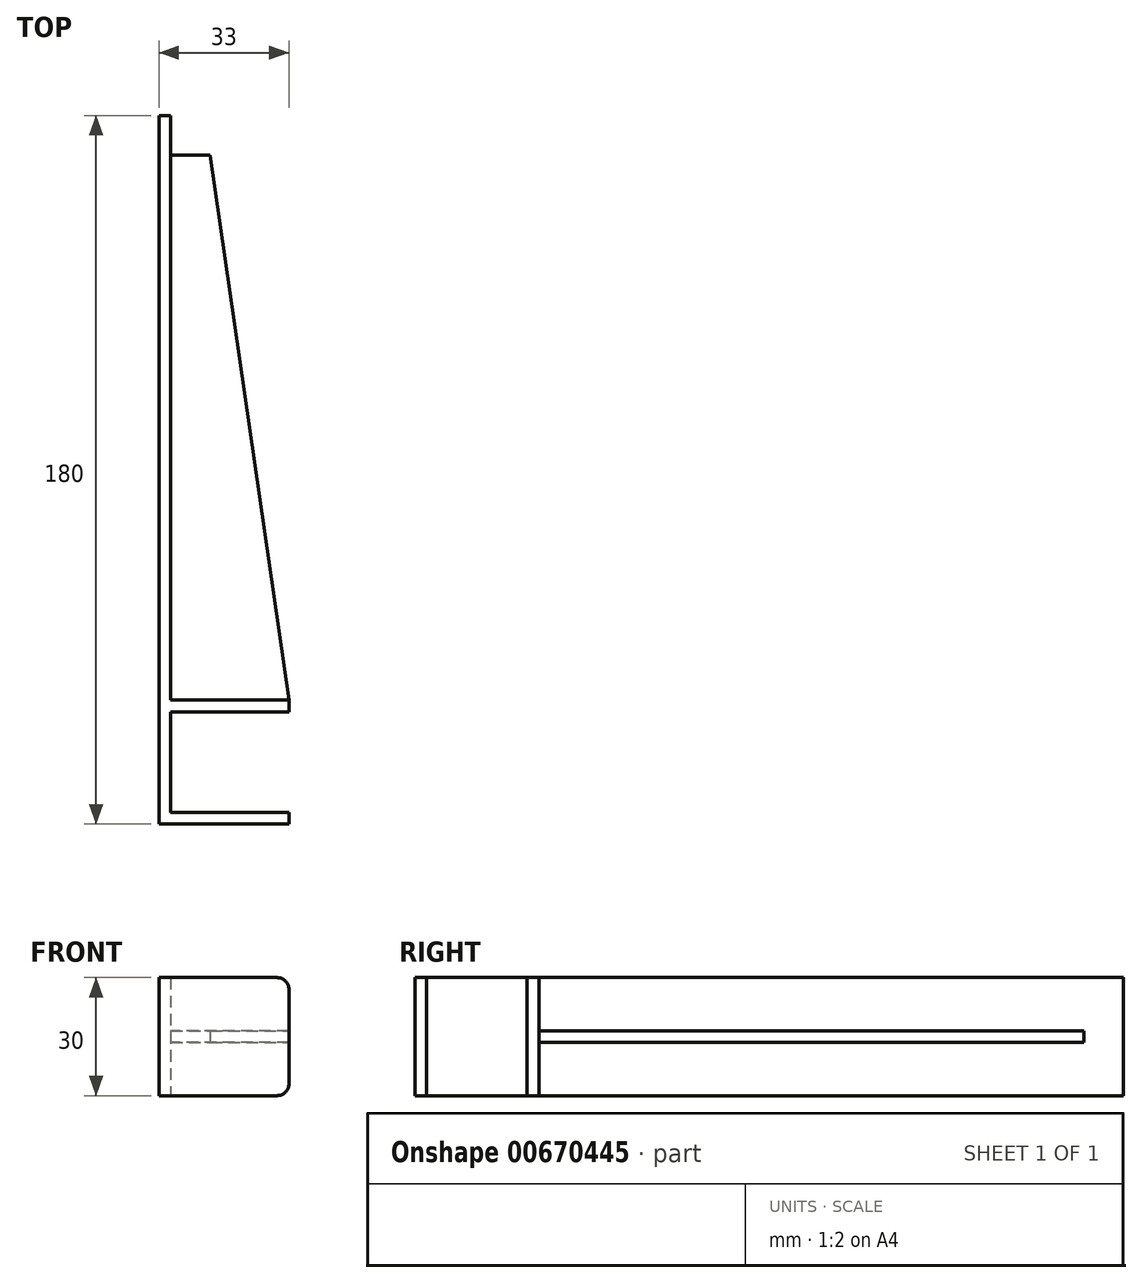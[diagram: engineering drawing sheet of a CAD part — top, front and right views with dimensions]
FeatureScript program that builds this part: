
annotation { "Feature Type Name" : "Feature", "Feature Type Description" : "" }
export const myFeature = defineFeature(function(context is Context, id is Id, definition is map)
    precondition{}
    {
        {
            var Q0;
            Q0=qCreatedBy(makeId("Top.planeOp"),FACE);
            var sketch = newSketch(context, id + "F0", { "sketchPlane" : qUnion([Q0])});
            skLineSegment(sketch, "E0", {"start": v(0, 0) * mm, "end": v(33, 0) * mm});
            skLineSegment(sketch, "E1", {"start": v(33, 0) * mm, "end": v(33, 3) * mm});
            skLineSegment(sketch, "E2", {"start": v(33, 3) * mm, "end": v(3, 3) * mm});
            skLineSegment(sketch, "E3", {"start": v(3, 3) * mm, "end": v(3, 28.5) * mm});
            skLineSegment(sketch, "E4", {"start": v(3, 28.5) * mm, "end": v(33, 28.5) * mm});
            skLineSegment(sketch, "E5", {"start": v(33, 28.5) * mm, "end": v(33, 31.5) * mm});
            skLineSegment(sketch, "E6", {"start": v(33, 31.5) * mm, "end": v(3, 31.5) * mm});
            skLineSegment(sketch, "E7", {"start": v(3, 31.5) * mm, "end": v(3, 180) * mm});
            skLineSegment(sketch, "E8", {"start": v(3, 180) * mm, "end": v(0, 180) * mm});
            skLineSegment(sketch, "E9", {"start": v(0, 180) * mm, "end": v(0, 0) * mm});
            skLineSegment(sketch, "E10", {"start": v(-10.93, 15.75) * mm, "end": v(35.26, 15.75) * mm, "construction": true});
            skPoint(sketch, "E10.startSnap0", {"position": v(3, 15.75) * mm});
            skSolve(sketch);
        }
        {
            var Q0;
            Q0 = qSketchRegion(id + "F0", true);
            extrude(context, id + "F1", {"entities" : qUnion([Q0]), "depth" : 30 * mm, "offsetDistance" : 25 * mm, "symmetric" : true});
        }
        {
            var Q0;
            Q0=qCreatedBy(makeId("Top.planeOp"),FACE);
            var sketch = newSketch(context, id + "F2", { "sketchPlane" : qUnion([Q0])});
            skLineSegment(sketch, "E11", {"start": v(33, 31.5) * mm, "end": v(3, 31.5) * mm});
            skLineSegment(sketch, "E12", {"start": v(3, 170) * mm, "end": v(13, 170) * mm});
            skLineSegment(sketch, "E13", {"start": v(3, 180) * mm, "end": v(-20.23, 180) * mm, "construction": true});
            skLineSegment(sketch, "E14", {"start": v(13, 170) * mm, "end": v(33, 31.5) * mm});
            skLineSegment(sketch, "E15", {"start": v(3, 170) * mm, "end": v(3, 31.5) * mm});
            skSolve(sketch);
        }
        {
            var Q0;
            Q0 = qSketchRegion(id + "F2", true);
            extrude(context, id + "F3", {"entities" : qUnion([Q0]), "depth" : 3 * mm, "offsetDistance" : 25 * mm, "symmetric" : true});
        }
        {
            var Q0;
            Q0=makeQuery(id+"F1.opExtrude","CAP_EDGE",EDGE,{"disambiguationData":[OSD([sQuery(id+"F0.wireOp",EDGE,"E5")])],"isStart":false});
            var Q1;
            Q1=makeQuery(id+"F1.opExtrude","CAP_EDGE",EDGE,{"disambiguationData":[OSD([sQuery(id+"F0.wireOp",EDGE,"E1")])],"isStart":false});
            var Q2;
            Q2=makeQuery(id+"F1.opExtrude","CAP_EDGE",EDGE,{"disambiguationData":[OSD([sQuery(id+"F0.wireOp",EDGE,"E5")])],"isStart":true});
            var Q3;
            Q3=makeQuery(id+"F1.opExtrude","CAP_EDGE",EDGE,{"disambiguationData":[OSD([sQuery(id+"F0.wireOp",EDGE,"E1")])],"isStart":true});
            fillet(context, id + "F4", {"entities" : qUnion([Q0, Q1, Q2, Q3]), "radius" : 3 * mm, "tangentPropagation" : true, "allowEdgeOverflow" : false});
        }
    });
